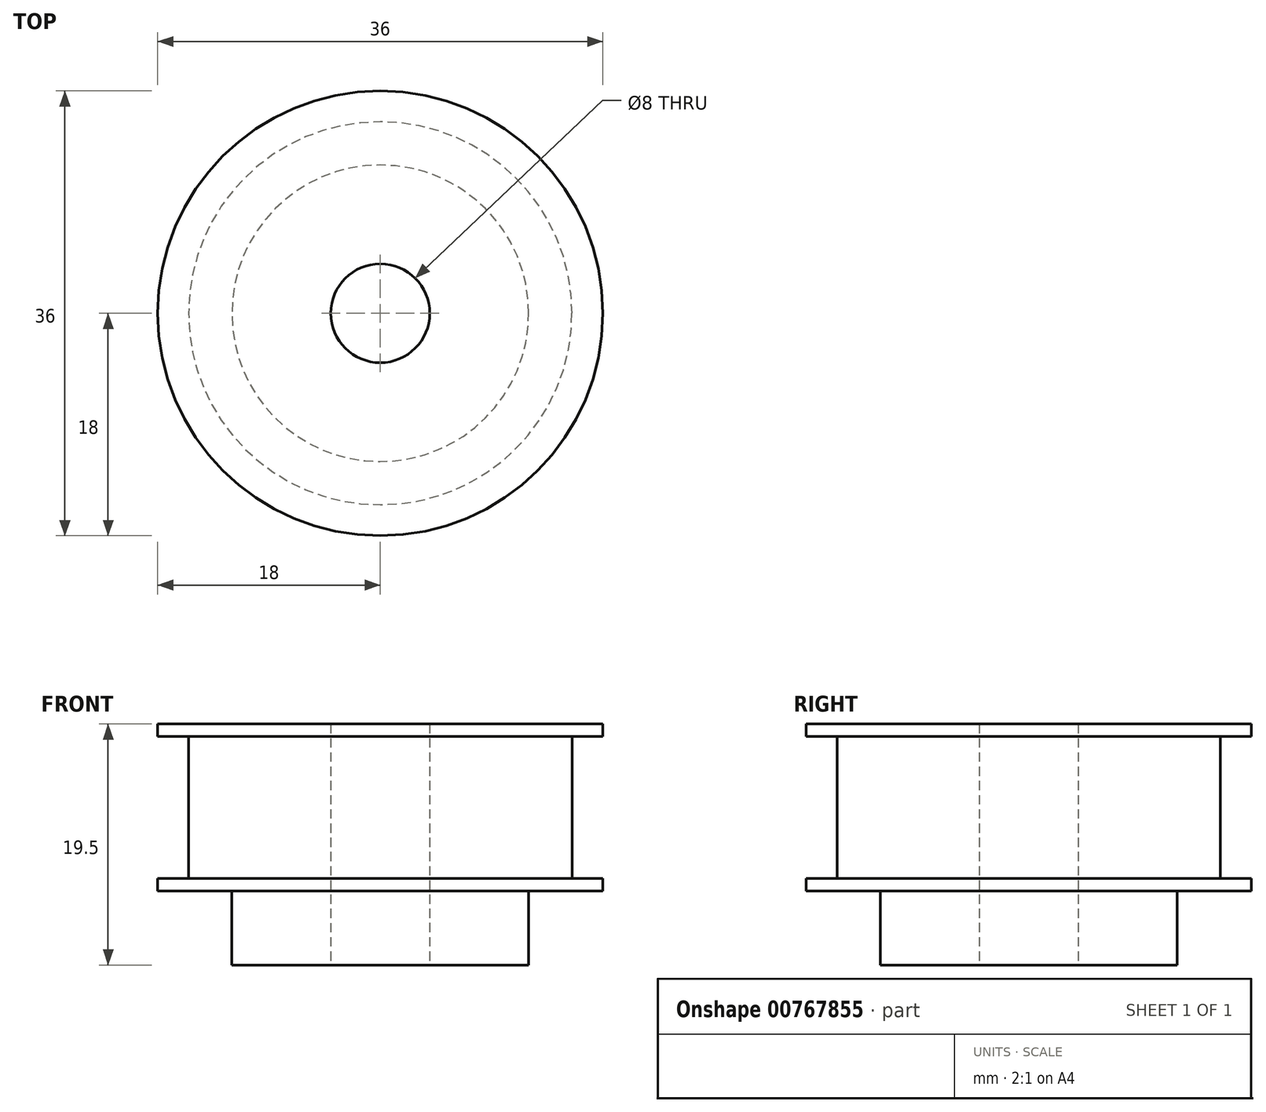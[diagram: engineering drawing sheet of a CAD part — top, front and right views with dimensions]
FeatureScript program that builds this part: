
annotation { "Feature Type Name" : "Feature", "Feature Type Description" : "" }
export const myFeature = defineFeature(function(context is Context, id is Id, definition is map)
    precondition{}
    {
        {
            var Q0;
            Q0=qCreatedBy(makeId("Top.planeOp"),FACE);
            var sketch = newSketch(context, id + "F0", { "sketchPlane" : qUnion([Q0])});
            skCircle(sketch, "E0", {"center": v(0, 0) * mm, "radius": 15.5 * mm});
            skSolve(sketch);
        }
        {
            var Q0;
            Q0=qSketchRegion(id+"F0",true);
            extrude(context, id + "F1", {"entities" : qUnion([Q0]), "depth" : 11.5 * mm, "offsetDistance" : 25 * mm});
        }
        {
            var Q0;
            Q0=makeQuery(id+"F1.opExtrude","CAP_FACE",FACE,{"disambiguationData":[OSD([sQuery(id+"F0.wireOp",EDGE,"E0")])],"isStart":false});
            var sketch = newSketch(context, id + "F2", { "sketchPlane" : qUnion([Q0])});
            skCircle(sketch, "E1", {"center": v(0, 0) * mm, "radius": 18 * mm});
            skSolve(sketch);
        }
        {
            var Q0;
            Q0=qSketchRegion(id+"F2",true);
            extrude(context, id + "F3", {"entities" : qUnion([Q0]), "operationType" : NewBodyOperationType.ADD, "depth" : 1 * mm, "offsetDistance" : 25 * mm});
        }
        {
            var Q0;
            Q0=qCreatedBy(makeId("Top.planeOp"),FACE);
            var sketch = newSketch(context, id + "F4", { "sketchPlane" : qUnion([Q0])});
            skCircle(sketch, "E2", {"center": v(0, 0) * mm, "radius": 18 * mm});
            skSolve(sketch);
        }
        {
            var Q0;
            Q0=makeQuery(id+"F4.imprint","IMPRINT",FACE,{"disambiguationData":[TD([[makeQuery(id+"F4.imprint","IMPRINT",EDGE,{"derivedFrom":sQuery(id+"F4.wireOp",EDGE,"E2")}),1.0]])]});
            var Q1;
            Q1=sQuery(id+"F4.wireOp",EDGE,"E2");
            extrude(context, id + "F5", {"entities" : qUnion([Q0]), "operationType" : NewBodyOperationType.ADD, "surfaceEntities" : qUnion([Q1]), "oppositeDirection" : true, "depth" : 1 * mm, "offsetDistance" : 25 * mm});
        }
        {
            var Q0;
            Q0=makeQuery(id+"F5.opExtrude","CAP_FACE",FACE,{"disambiguationData":[OSD([sQuery(id+"F4.wireOp",EDGE,"E2")])],"isStart":false});
            var sketch = newSketch(context, id + "F6", { "sketchPlane" : qUnion([Q0])});
            skCircle(sketch, "E3", {"center": v(0, 0) * mm, "radius": 12 * mm});
            skSolve(sketch);
        }
        {
            var Q0;
            Q0=qSketchRegion(id+"F6",true);
            extrude(context, id + "F7", {"entities" : qUnion([Q0]), "operationType" : NewBodyOperationType.ADD, "depth" : 6 * mm, "offsetDistance" : 25 * mm});
        }
        {
            var Q0;
            Q0=makeQuery(id+"F7.opExtrude","CAP_FACE",FACE,{"disambiguationData":[OSD([sQuery(id+"F6.wireOp",EDGE,"E3")])],"isStart":false});
            var sketch = newSketch(context, id + "F8", { "sketchPlane" : qUnion([Q0])});
            skCircle(sketch, "E4", {"center": v(0, 0) * mm, "radius": 4 * mm});
            skSolve(sketch);
        }
        {
            var Q0;
            Q0=qSketchRegion(id+"F8",true);
            extrude(context, id + "F9", {"entities" : qUnion([Q0]), "operationType" : NewBodyOperationType.REMOVE, "endBound" : BoundingType.THROUGH_ALL, "oppositeDirection" : true, "depth" : 25 * mm, "offsetDistance" : 25 * mm});
        }
    });
